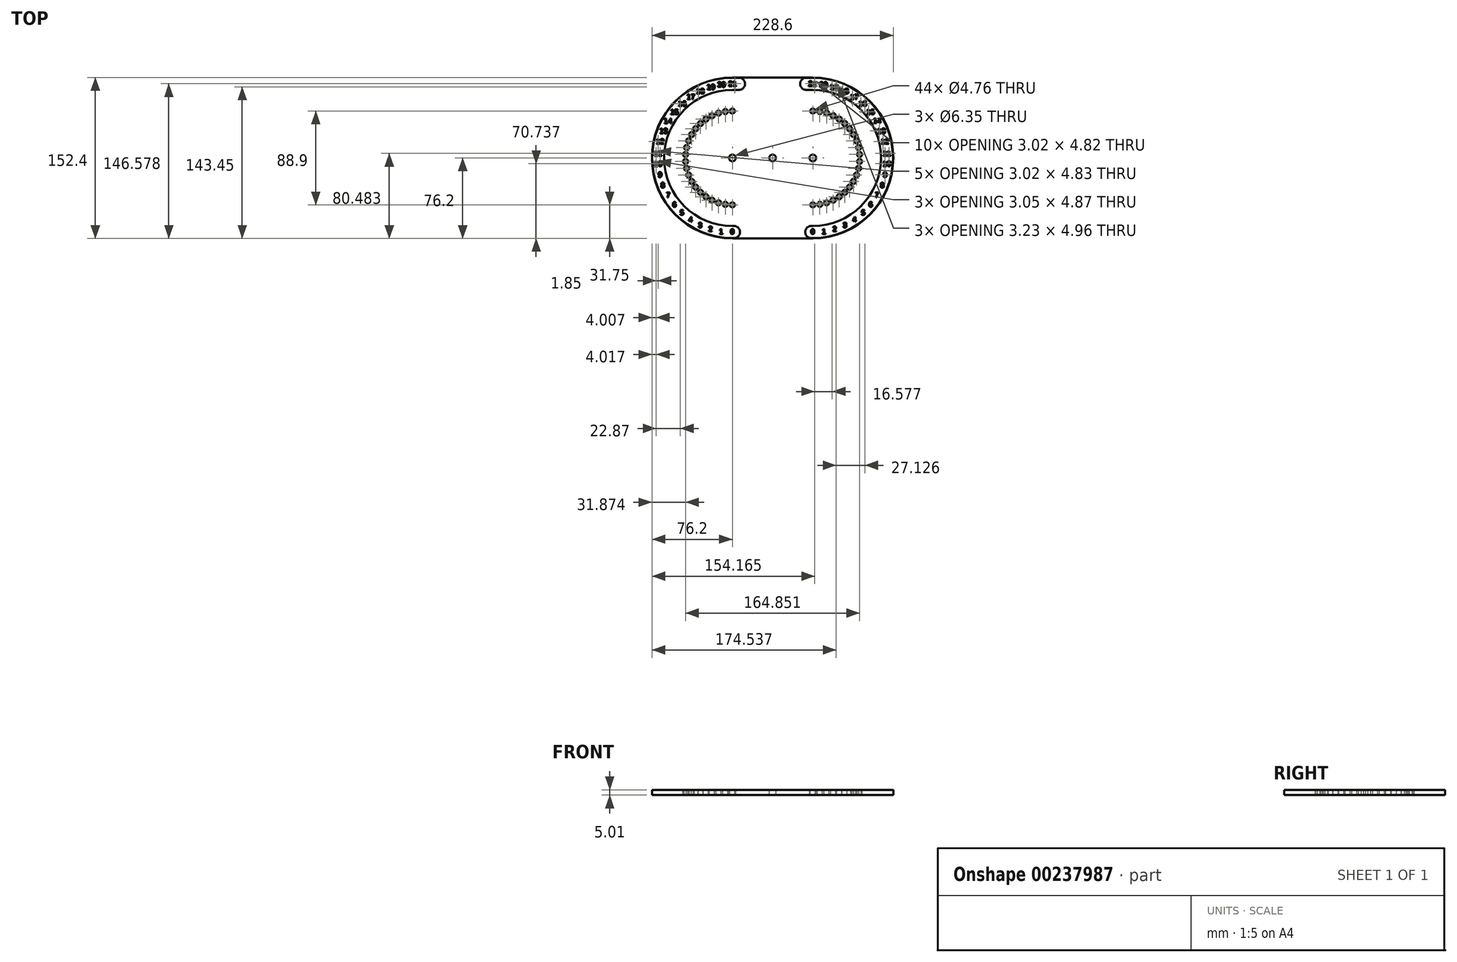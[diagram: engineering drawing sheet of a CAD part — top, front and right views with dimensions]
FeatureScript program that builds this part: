
annotation { "Feature Type Name" : "Feature", "Feature Type Description" : "" }
export const myFeature = defineFeature(function(context is Context, id is Id, definition is map)
    precondition{}
    {
        {
            var Q0;
            Q0=qCreatedBy(makeId("Top.planeOp"),FACE);
            var sketch = newSketch(context, id + "F0", { "sketchPlane" : qUnion([Q0])});
            skCircle(sketch, "E0", {"center": v(0, 0) * mm, "radius": 3.18 * mm});
            skLineSegment(sketch, "E1", {"start": v(0, 0) * mm, "end": v(38.1, 0) * mm, "construction": true});
            skLineSegment(sketch, "E2", {"start": v(0, 0) * mm, "end": v(-38.1, 0) * mm, "construction": true});
            skCircle(sketch, "E3", {"center": v(38.1, 0) * mm, "radius": 3.18 * mm});
            skCircle(sketch, "E4", {"center": v(-38.1, 0) * mm, "radius": 3.18 * mm});
            skCircle(sketch, "E5", {"center": v(38.1, 0) * mm, "radius": 44.45 * mm, "construction": true});
            skCircle(sketch, "E6", {"center": v(-38.1, 0) * mm, "radius": 44.45 * mm, "construction": true});
            skLineSegment(sketch, "E7.bottom", {"start": v(114.3, -76.2) * mm, "end": v(-114.3, -76.2) * mm});
            skLineSegment(sketch, "E7.top", {"start": v(114.3, 76.2) * mm, "end": v(-114.3, 76.2) * mm});
            skLineSegment(sketch, "E7.left", {"start": v(114.3, -76.2) * mm, "end": v(114.3, 76.2) * mm});
            skLineSegment(sketch, "E7.right", {"start": v(-114.3, -76.2) * mm, "end": v(-114.3, 76.2) * mm});
            skPoint(sketch, "E8", {"position": v(-114.3, 0) * mm});
            skSolve(sketch);
        }
        {
            var Q0;
            Q0 = qSketchRegion(id + "F0", true);
            extrude(context, id + "F1", {"entities" : qUnion([Q0]), "oppositeDirection" : true, "depth" : 4.76 * mm});
        }
        {
            var Q0;
            Q0=makeQuery(id+"F0.imprint","IMPRINT",FACE,{"disambiguationData":[TD([[makeQuery(id+"F0.imprint","IMPRINT",EDGE,{"derivedFrom":sQuery(id+"F0.wireOp",EDGE,"E0")}),-1.0]])]});
            var sketch = newSketch(context, id + "F2", { "sketchPlane" : qUnion([Q0])});
            skCircle(sketch, "E9", {"center": v(38.1, 44.45) * mm, "radius": 2.38 * mm});
            skLineSegment(sketch, "E10", {"start": v(38.1, 0) * mm, "end": v(38.1, 44.45) * mm, "construction": true});
            skSolve(sketch);
        }
        {
            var Q0;
            Q0 = qSketchRegion(id + "F2", true);
            extrude(context, id + "F3", {"entities" : qUnion([Q0]), "endBound" : BoundingType.SYMMETRIC, "oppositeDirection" : true, "depth" : 25.4 * mm});
        }
        {
            var Q0;
            Q0=makeQuery(id+"F3.opExtrude","SWEPT_BODY",BODY,{"disambiguationData":[OSD([sQuery(id+"F2.wireOp",EDGE,"E9")])]});
            var Q1;
            Q1=makeQuery(id+"F1.opExtrude","SWEPT_FACE",FACE,{"disambiguationData":[OSD([sQuery(id+"F0.wireOp",EDGE,"E3")])]});
            circularPattern(context, id + "F4", {"entities" : qUnion([Q0]), "axis" : qUnion([Q1]), "angle" : 180 * degree, "instanceCount" : 22, "equalSpace" : true});
        }
        {
            var Q0;
            Q0=makeQuery(id+"F4.opPattern","COPY",BODY,{"derivedFrom":makeQuery(id+"F3.opExtrude","SWEPT_BODY",BODY,{"disambiguationData":[OSD([sQuery(id+"F2.wireOp",EDGE,"E9")])]}),"instanceName":"10"});
            var Q1;
            Q1=makeQuery(id+"F4.opPattern","COPY",BODY,{"derivedFrom":makeQuery(id+"F3.opExtrude","SWEPT_BODY",BODY,{"disambiguationData":[OSD([sQuery(id+"F2.wireOp",EDGE,"E9")])]}),"instanceName":"11"});
            var Q2;
            Q2=makeQuery(id+"F4.opPattern","COPY",BODY,{"derivedFrom":makeQuery(id+"F3.opExtrude","SWEPT_BODY",BODY,{"disambiguationData":[OSD([sQuery(id+"F2.wireOp",EDGE,"E9")])]}),"instanceName":"12"});
            var Q3;
            Q3=makeQuery(id+"F4.opPattern","COPY",BODY,{"derivedFrom":makeQuery(id+"F3.opExtrude","SWEPT_BODY",BODY,{"disambiguationData":[OSD([sQuery(id+"F2.wireOp",EDGE,"E9")])]}),"instanceName":"13"});
            var Q4;
            Q4=makeQuery(id+"F4.opPattern","COPY",BODY,{"derivedFrom":makeQuery(id+"F3.opExtrude","SWEPT_BODY",BODY,{"disambiguationData":[OSD([sQuery(id+"F2.wireOp",EDGE,"E9")])]}),"instanceName":"14"});
            var Q5;
            Q5=makeQuery(id+"F4.opPattern","COPY",BODY,{"derivedFrom":makeQuery(id+"F3.opExtrude","SWEPT_BODY",BODY,{"disambiguationData":[OSD([sQuery(id+"F2.wireOp",EDGE,"E9")])]}),"instanceName":"15"});
            var Q6;
            Q6=makeQuery(id+"F4.opPattern","COPY",BODY,{"derivedFrom":makeQuery(id+"F3.opExtrude","SWEPT_BODY",BODY,{"disambiguationData":[OSD([sQuery(id+"F2.wireOp",EDGE,"E9")])]}),"instanceName":"16"});
            var Q7;
            Q7=makeQuery(id+"F4.opPattern","COPY",BODY,{"derivedFrom":makeQuery(id+"F3.opExtrude","SWEPT_BODY",BODY,{"disambiguationData":[OSD([sQuery(id+"F2.wireOp",EDGE,"E9")])]}),"instanceName":"17"});
            var Q8;
            Q8=makeQuery(id+"F4.opPattern","COPY",BODY,{"derivedFrom":makeQuery(id+"F3.opExtrude","SWEPT_BODY",BODY,{"disambiguationData":[OSD([sQuery(id+"F2.wireOp",EDGE,"E9")])]}),"instanceName":"18"});
            var Q9;
            Q9=makeQuery(id+"F4.opPattern","COPY",BODY,{"derivedFrom":makeQuery(id+"F3.opExtrude","SWEPT_BODY",BODY,{"disambiguationData":[OSD([sQuery(id+"F2.wireOp",EDGE,"E9")])]}),"instanceName":"19"});
            var Q10;
            Q10=makeQuery(id+"F4.opPattern","COPY",BODY,{"derivedFrom":makeQuery(id+"F3.opExtrude","SWEPT_BODY",BODY,{"disambiguationData":[OSD([sQuery(id+"F2.wireOp",EDGE,"E9")])]}),"instanceName":"20"});
            var Q11;
            Q11=makeQuery(id+"F4.opPattern","COPY",BODY,{"derivedFrom":makeQuery(id+"F3.opExtrude","SWEPT_BODY",BODY,{"disambiguationData":[OSD([sQuery(id+"F2.wireOp",EDGE,"E9")])]}),"instanceName":"1"});
            var Q12;
            Q12=makeQuery(id+"F3.opExtrude","SWEPT_BODY",BODY,{"disambiguationData":[OSD([sQuery(id+"F2.wireOp",EDGE,"E9")])]});
            var Q13;
            Q13=makeQuery(id+"F4.opPattern","COPY",BODY,{"derivedFrom":makeQuery(id+"F3.opExtrude","SWEPT_BODY",BODY,{"disambiguationData":[OSD([sQuery(id+"F2.wireOp",EDGE,"E9")])]}),"instanceName":"3"});
            var Q14;
            Q14=makeQuery(id+"F4.opPattern","COPY",BODY,{"derivedFrom":makeQuery(id+"F3.opExtrude","SWEPT_BODY",BODY,{"disambiguationData":[OSD([sQuery(id+"F2.wireOp",EDGE,"E9")])]}),"instanceName":"2"});
            var Q15;
            Q15=makeQuery(id+"F4.opPattern","COPY",BODY,{"derivedFrom":makeQuery(id+"F3.opExtrude","SWEPT_BODY",BODY,{"disambiguationData":[OSD([sQuery(id+"F2.wireOp",EDGE,"E9")])]}),"instanceName":"4"});
            var Q16;
            Q16=makeQuery(id+"F4.opPattern","COPY",BODY,{"derivedFrom":makeQuery(id+"F3.opExtrude","SWEPT_BODY",BODY,{"disambiguationData":[OSD([sQuery(id+"F2.wireOp",EDGE,"E9")])]}),"instanceName":"5"});
            var Q17;
            Q17=makeQuery(id+"F4.opPattern","COPY",BODY,{"derivedFrom":makeQuery(id+"F3.opExtrude","SWEPT_BODY",BODY,{"disambiguationData":[OSD([sQuery(id+"F2.wireOp",EDGE,"E9")])]}),"instanceName":"7"});
            var Q18;
            Q18=makeQuery(id+"F4.opPattern","COPY",BODY,{"derivedFrom":makeQuery(id+"F3.opExtrude","SWEPT_BODY",BODY,{"disambiguationData":[OSD([sQuery(id+"F2.wireOp",EDGE,"E9")])]}),"instanceName":"6"});
            var Q19;
            Q19=makeQuery(id+"F4.opPattern","COPY",BODY,{"derivedFrom":makeQuery(id+"F3.opExtrude","SWEPT_BODY",BODY,{"disambiguationData":[OSD([sQuery(id+"F2.wireOp",EDGE,"E9")])]}),"instanceName":"8"});
            var Q20;
            Q20=makeQuery(id+"F4.opPattern","COPY",BODY,{"derivedFrom":makeQuery(id+"F3.opExtrude","SWEPT_BODY",BODY,{"disambiguationData":[OSD([sQuery(id+"F2.wireOp",EDGE,"E9")])]}),"instanceName":"9"});
            var Q21;
            Q21=makeQuery(id+"F4.opPattern","COPY",BODY,{"derivedFrom":makeQuery(id+"F3.opExtrude","SWEPT_BODY",BODY,{"disambiguationData":[OSD([sQuery(id+"F2.wireOp",EDGE,"E9")])]}),"instanceName":"21"});
            var Q22;
            Q22=qCreatedBy(makeId("Right.planeOp"),FACE);
            mirror(context, id + "F5", {"entities" : qUnion([Q0, Q1, Q2, Q3, Q4, Q5, Q6, Q7, Q8, Q9, Q10, Q11, Q12, Q13, Q14, Q15, Q16, Q17, Q18, Q19, Q20, Q21]), "mirrorPlane" : qUnion([Q22])});
        }
        {
            var Q0;
            Q0=makeQuery(id+"F4.opPattern","COPY",BODY,{"derivedFrom":makeQuery(id+"F3.opExtrude","SWEPT_BODY",BODY,{"disambiguationData":[OSD([sQuery(id+"F2.wireOp",EDGE,"E9")])]}),"instanceName":"1"});
            var Q1;
            Q1=makeQuery(id+"F3.opExtrude","SWEPT_BODY",BODY,{"disambiguationData":[OSD([sQuery(id+"F2.wireOp",EDGE,"E9")])]});
            var Q2;
            Q2=makeQuery(id+"F4.opPattern","COPY",BODY,{"derivedFrom":makeQuery(id+"F3.opExtrude","SWEPT_BODY",BODY,{"disambiguationData":[OSD([sQuery(id+"F2.wireOp",EDGE,"E9")])]}),"instanceName":"3"});
            var Q3;
            Q3=makeQuery(id+"F4.opPattern","COPY",BODY,{"derivedFrom":makeQuery(id+"F3.opExtrude","SWEPT_BODY",BODY,{"disambiguationData":[OSD([sQuery(id+"F2.wireOp",EDGE,"E9")])]}),"instanceName":"2"});
            var Q4;
            Q4=makeQuery(id+"F4.opPattern","COPY",BODY,{"derivedFrom":makeQuery(id+"F3.opExtrude","SWEPT_BODY",BODY,{"disambiguationData":[OSD([sQuery(id+"F2.wireOp",EDGE,"E9")])]}),"instanceName":"4"});
            var Q5;
            Q5=makeQuery(id+"F4.opPattern","COPY",BODY,{"derivedFrom":makeQuery(id+"F3.opExtrude","SWEPT_BODY",BODY,{"disambiguationData":[OSD([sQuery(id+"F2.wireOp",EDGE,"E9")])]}),"instanceName":"5"});
            var Q6;
            Q6=makeQuery(id+"F5.opPattern","COPY",BODY,{"derivedFrom":makeQuery(id+"F4.opPattern","COPY",BODY,{"derivedFrom":makeQuery(id+"F3.opExtrude","SWEPT_BODY",BODY,{"disambiguationData":[OSD([sQuery(id+"F2.wireOp",EDGE,"E9")])]}),"instanceName":"3"}),"instanceName":"1"});
            var Q7;
            Q7=makeQuery(id+"F4.opPattern","COPY",BODY,{"derivedFrom":makeQuery(id+"F3.opExtrude","SWEPT_BODY",BODY,{"disambiguationData":[OSD([sQuery(id+"F2.wireOp",EDGE,"E9")])]}),"instanceName":"7"});
            var Q8;
            Q8=makeQuery(id+"F4.opPattern","COPY",BODY,{"derivedFrom":makeQuery(id+"F3.opExtrude","SWEPT_BODY",BODY,{"disambiguationData":[OSD([sQuery(id+"F2.wireOp",EDGE,"E9")])]}),"instanceName":"6"});
            var Q9;
            Q9=makeQuery(id+"F4.opPattern","COPY",BODY,{"derivedFrom":makeQuery(id+"F3.opExtrude","SWEPT_BODY",BODY,{"disambiguationData":[OSD([sQuery(id+"F2.wireOp",EDGE,"E9")])]}),"instanceName":"8"});
            var Q10;
            Q10=makeQuery(id+"F4.opPattern","COPY",BODY,{"derivedFrom":makeQuery(id+"F3.opExtrude","SWEPT_BODY",BODY,{"disambiguationData":[OSD([sQuery(id+"F2.wireOp",EDGE,"E9")])]}),"instanceName":"9"});
            var Q11;
            Q11=makeQuery(id+"F4.opPattern","COPY",BODY,{"derivedFrom":makeQuery(id+"F3.opExtrude","SWEPT_BODY",BODY,{"disambiguationData":[OSD([sQuery(id+"F2.wireOp",EDGE,"E9")])]}),"instanceName":"10"});
            var Q12;
            Q12=makeQuery(id+"F4.opPattern","COPY",BODY,{"derivedFrom":makeQuery(id+"F3.opExtrude","SWEPT_BODY",BODY,{"disambiguationData":[OSD([sQuery(id+"F2.wireOp",EDGE,"E9")])]}),"instanceName":"11"});
            var Q13;
            Q13=makeQuery(id+"F4.opPattern","COPY",BODY,{"derivedFrom":makeQuery(id+"F3.opExtrude","SWEPT_BODY",BODY,{"disambiguationData":[OSD([sQuery(id+"F2.wireOp",EDGE,"E9")])]}),"instanceName":"12"});
            var Q14;
            Q14=makeQuery(id+"F4.opPattern","COPY",BODY,{"derivedFrom":makeQuery(id+"F3.opExtrude","SWEPT_BODY",BODY,{"disambiguationData":[OSD([sQuery(id+"F2.wireOp",EDGE,"E9")])]}),"instanceName":"13"});
            var Q15;
            Q15=makeQuery(id+"F4.opPattern","COPY",BODY,{"derivedFrom":makeQuery(id+"F3.opExtrude","SWEPT_BODY",BODY,{"disambiguationData":[OSD([sQuery(id+"F2.wireOp",EDGE,"E9")])]}),"instanceName":"14"});
            var Q16;
            Q16=makeQuery(id+"F4.opPattern","COPY",BODY,{"derivedFrom":makeQuery(id+"F3.opExtrude","SWEPT_BODY",BODY,{"disambiguationData":[OSD([sQuery(id+"F2.wireOp",EDGE,"E9")])]}),"instanceName":"15"});
            var Q17;
            Q17=makeQuery(id+"F4.opPattern","COPY",BODY,{"derivedFrom":makeQuery(id+"F3.opExtrude","SWEPT_BODY",BODY,{"disambiguationData":[OSD([sQuery(id+"F2.wireOp",EDGE,"E9")])]}),"instanceName":"16"});
            var Q18;
            Q18=makeQuery(id+"F4.opPattern","COPY",BODY,{"derivedFrom":makeQuery(id+"F3.opExtrude","SWEPT_BODY",BODY,{"disambiguationData":[OSD([sQuery(id+"F2.wireOp",EDGE,"E9")])]}),"instanceName":"17"});
            var Q19;
            Q19=makeQuery(id+"F4.opPattern","COPY",BODY,{"derivedFrom":makeQuery(id+"F3.opExtrude","SWEPT_BODY",BODY,{"disambiguationData":[OSD([sQuery(id+"F2.wireOp",EDGE,"E9")])]}),"instanceName":"18"});
            var Q20;
            Q20=makeQuery(id+"F4.opPattern","COPY",BODY,{"derivedFrom":makeQuery(id+"F3.opExtrude","SWEPT_BODY",BODY,{"disambiguationData":[OSD([sQuery(id+"F2.wireOp",EDGE,"E9")])]}),"instanceName":"19"});
            var Q21;
            Q21=makeQuery(id+"F4.opPattern","COPY",BODY,{"derivedFrom":makeQuery(id+"F3.opExtrude","SWEPT_BODY",BODY,{"disambiguationData":[OSD([sQuery(id+"F2.wireOp",EDGE,"E9")])]}),"instanceName":"20"});
            var Q22;
            Q22=makeQuery(id+"F5.opPattern","COPY",BODY,{"derivedFrom":makeQuery(id+"F4.opPattern","COPY",BODY,{"derivedFrom":makeQuery(id+"F3.opExtrude","SWEPT_BODY",BODY,{"disambiguationData":[OSD([sQuery(id+"F2.wireOp",EDGE,"E9")])]}),"instanceName":"2"}),"instanceName":"1"});
            var Q23;
            Q23=makeQuery(id+"F5.opPattern","COPY",BODY,{"derivedFrom":makeQuery(id+"F4.opPattern","COPY",BODY,{"derivedFrom":makeQuery(id+"F3.opExtrude","SWEPT_BODY",BODY,{"disambiguationData":[OSD([sQuery(id+"F2.wireOp",EDGE,"E9")])]}),"instanceName":"1"}),"instanceName":"1"});
            var Q24;
            Q24=makeQuery(id+"F5.opPattern","COPY",BODY,{"derivedFrom":makeQuery(id+"F4.opPattern","COPY",BODY,{"derivedFrom":makeQuery(id+"F3.opExtrude","SWEPT_BODY",BODY,{"disambiguationData":[OSD([sQuery(id+"F2.wireOp",EDGE,"E9")])]}),"instanceName":"4"}),"instanceName":"1"});
            var Q25;
            Q25=makeQuery(id+"F5.opPattern","COPY",BODY,{"derivedFrom":makeQuery(id+"F4.opPattern","COPY",BODY,{"derivedFrom":makeQuery(id+"F3.opExtrude","SWEPT_BODY",BODY,{"disambiguationData":[OSD([sQuery(id+"F2.wireOp",EDGE,"E9")])]}),"instanceName":"5"}),"instanceName":"1"});
            var Q26;
            Q26=makeQuery(id+"F5.opPattern","COPY",BODY,{"derivedFrom":makeQuery(id+"F4.opPattern","COPY",BODY,{"derivedFrom":makeQuery(id+"F3.opExtrude","SWEPT_BODY",BODY,{"disambiguationData":[OSD([sQuery(id+"F2.wireOp",EDGE,"E9")])]}),"instanceName":"6"}),"instanceName":"1"});
            var Q27;
            Q27=makeQuery(id+"F5.opPattern","COPY",BODY,{"derivedFrom":makeQuery(id+"F4.opPattern","COPY",BODY,{"derivedFrom":makeQuery(id+"F3.opExtrude","SWEPT_BODY",BODY,{"disambiguationData":[OSD([sQuery(id+"F2.wireOp",EDGE,"E9")])]}),"instanceName":"10"}),"instanceName":"1"});
            var Q28;
            Q28=makeQuery(id+"F5.opPattern","COPY",BODY,{"derivedFrom":makeQuery(id+"F4.opPattern","COPY",BODY,{"derivedFrom":makeQuery(id+"F3.opExtrude","SWEPT_BODY",BODY,{"disambiguationData":[OSD([sQuery(id+"F2.wireOp",EDGE,"E9")])]}),"instanceName":"11"}),"instanceName":"1"});
            var Q29;
            Q29=makeQuery(id+"F5.opPattern","COPY",BODY,{"derivedFrom":makeQuery(id+"F4.opPattern","COPY",BODY,{"derivedFrom":makeQuery(id+"F3.opExtrude","SWEPT_BODY",BODY,{"disambiguationData":[OSD([sQuery(id+"F2.wireOp",EDGE,"E9")])]}),"instanceName":"12"}),"instanceName":"1"});
            var Q30;
            Q30=makeQuery(id+"F5.opPattern","COPY",BODY,{"derivedFrom":makeQuery(id+"F4.opPattern","COPY",BODY,{"derivedFrom":makeQuery(id+"F3.opExtrude","SWEPT_BODY",BODY,{"disambiguationData":[OSD([sQuery(id+"F2.wireOp",EDGE,"E9")])]}),"instanceName":"13"}),"instanceName":"1"});
            var Q31;
            Q31=makeQuery(id+"F5.opPattern","COPY",BODY,{"derivedFrom":makeQuery(id+"F4.opPattern","COPY",BODY,{"derivedFrom":makeQuery(id+"F3.opExtrude","SWEPT_BODY",BODY,{"disambiguationData":[OSD([sQuery(id+"F2.wireOp",EDGE,"E9")])]}),"instanceName":"14"}),"instanceName":"1"});
            var Q32;
            Q32=makeQuery(id+"F5.opPattern","COPY",BODY,{"derivedFrom":makeQuery(id+"F4.opPattern","COPY",BODY,{"derivedFrom":makeQuery(id+"F3.opExtrude","SWEPT_BODY",BODY,{"disambiguationData":[OSD([sQuery(id+"F2.wireOp",EDGE,"E9")])]}),"instanceName":"15"}),"instanceName":"1"});
            var Q33;
            Q33=makeQuery(id+"F5.opPattern","COPY",BODY,{"derivedFrom":makeQuery(id+"F4.opPattern","COPY",BODY,{"derivedFrom":makeQuery(id+"F3.opExtrude","SWEPT_BODY",BODY,{"disambiguationData":[OSD([sQuery(id+"F2.wireOp",EDGE,"E9")])]}),"instanceName":"16"}),"instanceName":"1"});
            var Q34;
            Q34=makeQuery(id+"F5.opPattern","COPY",BODY,{"derivedFrom":makeQuery(id+"F4.opPattern","COPY",BODY,{"derivedFrom":makeQuery(id+"F3.opExtrude","SWEPT_BODY",BODY,{"disambiguationData":[OSD([sQuery(id+"F2.wireOp",EDGE,"E9")])]}),"instanceName":"17"}),"instanceName":"1"});
            var Q35;
            Q35=makeQuery(id+"F5.opPattern","COPY",BODY,{"derivedFrom":makeQuery(id+"F4.opPattern","COPY",BODY,{"derivedFrom":makeQuery(id+"F3.opExtrude","SWEPT_BODY",BODY,{"disambiguationData":[OSD([sQuery(id+"F2.wireOp",EDGE,"E9")])]}),"instanceName":"18"}),"instanceName":"1"});
            var Q36;
            Q36=makeQuery(id+"F5.opPattern","COPY",BODY,{"derivedFrom":makeQuery(id+"F4.opPattern","COPY",BODY,{"derivedFrom":makeQuery(id+"F3.opExtrude","SWEPT_BODY",BODY,{"disambiguationData":[OSD([sQuery(id+"F2.wireOp",EDGE,"E9")])]}),"instanceName":"19"}),"instanceName":"1"});
            var Q37;
            Q37=makeQuery(id+"F5.opPattern","COPY",BODY,{"derivedFrom":makeQuery(id+"F4.opPattern","COPY",BODY,{"derivedFrom":makeQuery(id+"F3.opExtrude","SWEPT_BODY",BODY,{"disambiguationData":[OSD([sQuery(id+"F2.wireOp",EDGE,"E9")])]}),"instanceName":"20"}),"instanceName":"1"});
            var Q38;
            Q38=makeQuery(id+"F5.opPattern","COPY",BODY,{"derivedFrom":makeQuery(id+"F3.opExtrude","SWEPT_BODY",BODY,{"disambiguationData":[OSD([sQuery(id+"F2.wireOp",EDGE,"E9")])]}),"instanceName":"1"});
            var Q39;
            Q39=makeQuery(id+"F5.opPattern","COPY",BODY,{"derivedFrom":makeQuery(id+"F4.opPattern","COPY",BODY,{"derivedFrom":makeQuery(id+"F3.opExtrude","SWEPT_BODY",BODY,{"disambiguationData":[OSD([sQuery(id+"F2.wireOp",EDGE,"E9")])]}),"instanceName":"7"}),"instanceName":"1"});
            var Q40;
            Q40=makeQuery(id+"F5.opPattern","COPY",BODY,{"derivedFrom":makeQuery(id+"F4.opPattern","COPY",BODY,{"derivedFrom":makeQuery(id+"F3.opExtrude","SWEPT_BODY",BODY,{"disambiguationData":[OSD([sQuery(id+"F2.wireOp",EDGE,"E9")])]}),"instanceName":"8"}),"instanceName":"1"});
            var Q41;
            Q41=makeQuery(id+"F5.opPattern","COPY",BODY,{"derivedFrom":makeQuery(id+"F4.opPattern","COPY",BODY,{"derivedFrom":makeQuery(id+"F3.opExtrude","SWEPT_BODY",BODY,{"disambiguationData":[OSD([sQuery(id+"F2.wireOp",EDGE,"E9")])]}),"instanceName":"9"}),"instanceName":"1"});
            var Q42;
            Q42=makeQuery(id+"F4.opPattern","COPY",BODY,{"derivedFrom":makeQuery(id+"F3.opExtrude","SWEPT_BODY",BODY,{"disambiguationData":[OSD([sQuery(id+"F2.wireOp",EDGE,"E9")])]}),"instanceName":"21"});
            var Q43;
            Q43=makeQuery(id+"F5.opPattern","COPY",BODY,{"derivedFrom":makeQuery(id+"F4.opPattern","COPY",BODY,{"derivedFrom":makeQuery(id+"F3.opExtrude","SWEPT_BODY",BODY,{"disambiguationData":[OSD([sQuery(id+"F2.wireOp",EDGE,"E9")])]}),"instanceName":"21"}),"instanceName":"1"});
            var Q44;
            Q44=makeQuery(id+"F1.opExtrude","SWEPT_BODY",BODY,{"disambiguationData":[OSD([sQuery(id+"F0.wireOp",EDGE,"E0"),sQuery(id+"F0.wireOp",EDGE,"E3"),sQuery(id+"F0.wireOp",EDGE,"E4"),sQuery(id+"F0.wireOp",EDGE,"E7.bottom"),sQuery(id+"F0.wireOp",EDGE,"E7.top"),sQuery(id+"F0.wireOp",EDGE,"E7.left"),sQuery(id+"F0.wireOp",EDGE,"E7.right")])]});
            booleanBodies(context, id + "F6", {"operationType" : BooleanOperationType.SUBTRACTION, "tools" : qUnion([Q0, Q1, Q2, Q3, Q4, Q5, Q6, Q7, Q8, Q9, Q10, Q11, Q12, Q13, Q14, Q15, Q16, Q17, Q18, Q19, Q20, Q21, Q22, Q23, Q24, Q25, Q26, Q27, Q28, Q29, Q30, Q31, Q32, Q33, Q34, Q35, Q36, Q37, Q38, Q39, Q40, Q41, Q42, Q43]), "targets" : qUnion([Q44])});
        }
        {
            var Q0;
            Q0=makeQuery(id+"F1.opExtrude","SWEPT_EDGE",EDGE,{"disambiguationData":[OSD([sQuery(id+"F0.wireOp",EDGE,"E7.bottom"),sQuery(id+"F0.wireOp",EDGE,"E7.right")])]});
            var Q1;
            Q1=makeQuery(id+"F1.opExtrude","SWEPT_EDGE",EDGE,{"disambiguationData":[OSD([sQuery(id+"F0.wireOp",EDGE,"E7.top"),sQuery(id+"F0.wireOp",EDGE,"E7.right")])]});
            var Q2;
            Q2=makeQuery(id+"F1.opExtrude","SWEPT_EDGE",EDGE,{"disambiguationData":[OSD([sQuery(id+"F0.wireOp",EDGE,"E7.top"),sQuery(id+"F0.wireOp",EDGE,"E7.left")])]});
            var Q3;
            Q3=makeQuery(id+"F1.opExtrude","SWEPT_EDGE",EDGE,{"disambiguationData":[OSD([sQuery(id+"F0.wireOp",EDGE,"E7.bottom"),sQuery(id+"F0.wireOp",EDGE,"E7.left")])]});
            fillet(context, id + "F7", {"entities" : qUnion([Q0, Q1, Q2, Q3]), "radius" : 76.2 * mm, "tangentPropagation" : true, "allowEdgeOverflow" : false});
        }
        {
            var Q0;
            Q0=makeQuery(id+"F1.opExtrude","CAP_FACE",FACE,{"disambiguationData":[OSD([sQuery(id+"F0.wireOp",EDGE,"E0"),sQuery(id+"F0.wireOp",EDGE,"E3"),sQuery(id+"F0.wireOp",EDGE,"E4"),sQuery(id+"F0.wireOp",EDGE,"E7.bottom"),sQuery(id+"F0.wireOp",EDGE,"E7.top"),sQuery(id+"F0.wireOp",EDGE,"E7.left"),sQuery(id+"F0.wireOp",EDGE,"E7.right")])],"isStart":true});
            var sketch = newSketch(context, id + "F8", { "sketchPlane" : qUnion([Q0])});
            skText(sketch, "E11", { "text": "21", "fontName": "Arimo-Regular.ttf"});
            skText(sketch, "E12", { "text": "20", "fontName": "Arimo-Regular.ttf"});
            skText(sketch, "E13", { "text": "19", "fontName": "Arimo-Regular.ttf"});
            skText(sketch, "E14", { "text": "17", "fontName": "Arimo-Regular.ttf"});
            skText(sketch, "E15", { "text": "14", "fontName": "Arimo-Regular.ttf"});
            skText(sketch, "E16", { "text": "15", "fontName": "Arimo-Regular.ttf"});
            skText(sketch, "E17", { "text": "7", "fontName": "Arimo-Regular.ttf"});
            skText(sketch, "E18", { "text": "13", "fontName": "Arimo-Regular.ttf"});
            skText(sketch, "E19", { "text": "18\n", "fontName": "Arimo-Regular.ttf"});
            skText(sketch, "E20", { "text": "8", "fontName": "Arimo-Regular.ttf"});
            skText(sketch, "E21", { "text": "16", "fontName": "Arimo-Regular.ttf"});
            skText(sketch, "E22", { "text": "11", "fontName": "Arimo-Regular.ttf"});
            skText(sketch, "E23", { "text": "9", "fontName": "Arimo-Regular.ttf"});
            skText(sketch, "E24", { "text": "12", "fontName": "Arimo-Regular.ttf"});
            skText(sketch, "E25", { "text": "10", "fontName": "Arimo-Regular.ttf"});
            skText(sketch, "E26", { "text": "0", "fontName": "Arimo-Regular.ttf"});
            skText(sketch, "E27", { "text": "4", "fontName": "Arimo-Regular.ttf"});
            skText(sketch, "E28", { "text": "2", "fontName": "Arimo-Regular.ttf"});
            skText(sketch, "E29", { "text": "6", "fontName": "Arimo-Regular.ttf"});
            skText(sketch, "E30", { "text": "3", "fontName": "Arimo-Regular.ttf"});
            skText(sketch, "E31", { "text": "1", "fontName": "Arimo-Regular.ttf"});
            skText(sketch, "E32", { "text": "5", "fontName": "Arimo-Regular.ttf"});
            skArc(sketch, "E33.0", {"start": v(38.1, -75.95) * mm, "mid": v(114.05, 0) * mm, "end": v(38.1, 75.95) * mm});
            skLineSegment(sketch, "E34", {"start": v(38.1, 75.95) * mm, "end": v(31.75, 75.95) * mm});
            skLineSegment(sketch, "E35", {"start": v(38.1, -75.95) * mm, "end": v(36.58, -75.95) * mm});
            skLineSegment(sketch, "E36.0", {"start": v(38.1, -64.52) * mm, "end": v(36.58, -64.52) * mm});
            skArc(sketch, "E36.1", {"start": v(38.1, -64.52) * mm, "mid": v(102.62, 0) * mm, "end": v(38.1, 64.52) * mm});
            skLineSegment(sketch, "E36.2", {"start": v(38.1, 64.52) * mm, "end": v(31.75, 64.52) * mm});
            skArc(sketch, "E37", {"start": v(31.75, 75.95) * mm, "mid": v(26.04, 70.23) * mm, "end": v(31.75, 64.52) * mm});
            skArc(sketch, "E38", {"start": v(36.58, -64.52) * mm, "mid": v(30.86, -70.23) * mm, "end": v(36.58, -75.95) * mm});
            skLineSegment(sketch, "E39", {"start": v(38.1, 0) * mm, "end": v(38.1, 44.45) * mm, "construction": true});
            skLineSegment(sketch, "E40", {"start": v(38.1, 0) * mm, "end": v(44.72, 43.95) * mm, "construction": true});
            skLineSegment(sketch, "E41", {"start": v(38.1, 0) * mm, "end": v(51.2, 42.48) * mm, "construction": true});
            skLineSegment(sketch, "E42", {"start": v(51.2, 42.48) * mm, "end": v(60.49, 72.57) * mm, "construction": true});
            skLineSegment(sketch, "E43", {"start": v(38.1, 0) * mm, "end": v(57.39, 40.05) * mm, "construction": true});
            skLineSegment(sketch, "E44", {"start": v(57.39, 40.05) * mm, "end": v(71.05, 68.42) * mm, "construction": true});
            skLineSegment(sketch, "E45", {"start": v(38.1, 0) * mm, "end": v(63.14, 36.73) * mm, "construction": true});
            skLineSegment(sketch, "E46", {"start": v(63.14, 36.73) * mm, "end": v(80.88, 62.75) * mm, "construction": true});
            skLineSegment(sketch, "E47", {"start": v(38.1, 0) * mm, "end": v(68.33, 32.58) * mm, "construction": true});
            skLineSegment(sketch, "E48", {"start": v(68.33, 32.58) * mm, "end": v(89.76, 55.67) * mm, "construction": true});
            skLineSegment(sketch, "E49", {"start": v(38.1, 0) * mm, "end": v(72.85, 27.71) * mm, "construction": true});
            skLineSegment(sketch, "E50", {"start": v(72.85, 27.71) * mm, "end": v(97.48, 47.35) * mm, "construction": true});
            skLineSegment(sketch, "E51", {"start": v(38.1, 0) * mm, "end": v(76.6, 22.23) * mm, "construction": true});
            skLineSegment(sketch, "E52", {"start": v(76.6, 22.22) * mm, "end": v(103.87, 37.97) * mm, "construction": true});
            skLineSegment(sketch, "E53", {"start": v(38.1, 0) * mm, "end": v(79.48, 16.24) * mm, "construction": true});
            skLineSegment(sketch, "E54", {"start": v(79.48, 16.24) * mm, "end": v(108.8, 27.75) * mm, "construction": true});
            skLineSegment(sketch, "E55", {"start": v(38.1, 0) * mm, "end": v(81.44, 9.9) * mm, "construction": true});
            skLineSegment(sketch, "E56", {"start": v(81.44, 9.9) * mm, "end": v(112.14, 16.9) * mm, "construction": true});
            skLineSegment(sketch, "E57", {"start": v(38.1, 0) * mm, "end": v(82.43, 3.32) * mm, "construction": true});
            skLineSegment(sketch, "E58", {"start": v(82.43, 3.32) * mm, "end": v(113.83, 5.68) * mm, "construction": true});
            skLineSegment(sketch, "E59", {"start": v(38.1, 0) * mm, "end": v(82.43, -3.32) * mm, "construction": true});
            skLineSegment(sketch, "E60", {"start": v(82.43, -3.32) * mm, "end": v(113.83, -5.68) * mm, "construction": true});
            skLineSegment(sketch, "E61", {"start": v(38.1, 0) * mm, "end": v(81.44, -9.9) * mm, "construction": true});
            skLineSegment(sketch, "E62", {"start": v(81.44, -9.9) * mm, "end": v(112.14, -16.9) * mm, "construction": true});
            skLineSegment(sketch, "E63", {"start": v(38.1, 0) * mm, "end": v(79.48, -16.24) * mm, "construction": true});
            skLineSegment(sketch, "E64", {"start": v(79.48, -16.24) * mm, "end": v(108.8, -27.75) * mm, "construction": true});
            skLineSegment(sketch, "E65", {"start": v(38.1, 0) * mm, "end": v(76.6, -22.23) * mm, "construction": true});
            skLineSegment(sketch, "E66", {"start": v(76.6, -22.23) * mm, "end": v(103.87, -37.97) * mm, "construction": true});
            skLineSegment(sketch, "E67", {"start": v(38.1, 0) * mm, "end": v(72.85, -27.71) * mm, "construction": true});
            skLineSegment(sketch, "E68", {"start": v(72.85, -27.71) * mm, "end": v(97.48, -47.35) * mm, "construction": true});
            skLineSegment(sketch, "E69", {"start": v(38.1, 0) * mm, "end": v(68.33, -32.58) * mm, "construction": true});
            skLineSegment(sketch, "E70", {"start": v(68.33, -32.58) * mm, "end": v(89.76, -55.67) * mm, "construction": true});
            skLineSegment(sketch, "E71", {"start": v(38.1, 0) * mm, "end": v(63.14, -36.73) * mm, "construction": true});
            skLineSegment(sketch, "E72", {"start": v(63.14, -36.73) * mm, "end": v(80.88, -62.75) * mm, "construction": true});
            skLineSegment(sketch, "E73", {"start": v(38.1, 0) * mm, "end": v(57.39, -40.05) * mm, "construction": true});
            skLineSegment(sketch, "E74", {"start": v(57.39, -40.05) * mm, "end": v(71.05, -68.42) * mm, "construction": true});
            skLineSegment(sketch, "E75", {"start": v(38.1, 0) * mm, "end": v(51.2, -42.48) * mm, "construction": true});
            skLineSegment(sketch, "E76", {"start": v(51.2, -42.48) * mm, "end": v(60.49, -72.57) * mm, "construction": true});
            skLineSegment(sketch, "E77", {"start": v(38.1, 0) * mm, "end": v(44.72, -43.95) * mm, "construction": true});
            skLineSegment(sketch, "E78", {"start": v(44.72, -43.95) * mm, "end": v(49.42, -75.1) * mm, "construction": true});
            skLineSegment(sketch, "E79", {"start": v(38.1, 0) * mm, "end": v(38.1, -44.45) * mm, "construction": true});
            skLineSegment(sketch, "E80", {"start": v(38.1, -44.45) * mm, "end": v(38.1, -75.95) * mm, "construction": true});
            skLineSegment(sketch, "E81", {"start": v(44.72, 43.95) * mm, "end": v(49.42, 75.1) * mm, "construction": true});
            skLineSegment(sketch, "E82", {"start": v(38.1, 44.45) * mm, "end": v(38.1, 75.95) * mm, "construction": true});
            const initialGuessF8  = {"E11": [0.03393, 0.06797, 1, 0, 0.00504], "E12": [0.04434, 0.06718, 1, 0, 0.005], "E13": [0.0544, 0.06484, 1, 0, 0.00504], "E14": [0.07357, 0.05546, 1, 0, 0.00504], "E15": [0.09513, 0.03284, 1, 0, 0.00496], "E16": [0.08891, 0.04127, 1, 0, 0.00504], "E17": [0.0968, -0.03738, 1, 0, 0.00497], "E18": [0.0992, 0.0232, 1, 0, 0.00504], "E19": [0.06436, 0.06093, 1, 0, 0.00504], "E20": [0.102, -0.0281, 1, 0, 0.0049], "E21": [0.0815, 0.04909, 1, 0, 0.00504], "E22": [0.10442, 0.0019, 1, 0, 0.00504], "E23": [0.10457, -0.01825, 1, 0, 0.00504], "E24": [0.10256, 0.0132, 1, 0, 0.00505], "E25": [0.10436, -0.00786, 1, 0, 0.00504], "E26": [0.03612, -0.07208, 1, 0, 0.00487], "E27": [0.0758, -0.0606, 1, 0, 0.0048], "E28": [0.05683, -0.06966, 1, 0, 0.00497], "E29": [0.09098, -0.04641, 1, 0, 0.00491], "E30": [0.06662, -0.06592, 1, 0, 0.00491], "E31": [0.04676, -0.07208, 1, 0, 0.00495], "E32": [0.0839, -0.05405, 1, 0, 0.0049]};
            skSetInitialGuess(sketch, initialGuessF8);
            skSolve(sketch);
        }
        {
            var Q0;
            Q0 = qSketchRegion(id + "F8", true);
            var Q1;
            Q1=makeQuery(id+"F8.imprint","IMPRINT",FACE,{"disambiguationData":[TD([[makeQuery(id+"F8.imprint","IMPRINT",EDGE,{"derivedFrom":sQuery(id+"F8.wireOp",EDGE,"E12.sketch_text.stroke-32")}),1.0]])]});
            var Q2;
            Q2=makeQuery(id+"F8.imprint","IMPRINT",FACE,{"disambiguationData":[TD([[makeQuery(id+"F8.imprint","IMPRINT",EDGE,{"derivedFrom":sQuery(id+"F8.wireOp",EDGE,"E13.sketch_text.stroke-27")}),1.0]])]});
            var Q3;
            Q3=makeQuery(id+"F8.imprint","IMPRINT",FACE,{"disambiguationData":[TD([[makeQuery(id+"F8.imprint","IMPRINT",EDGE,{"derivedFrom":sQuery(id+"F8.wireOp",EDGE,"E19.sketch_text.stroke-29")}),1.0]])]});
            var Q4;
            Q4=makeQuery(id+"F8.imprint","IMPRINT",FACE,{"disambiguationData":[TD([[makeQuery(id+"F8.imprint","IMPRINT",EDGE,{"derivedFrom":sQuery(id+"F8.wireOp",EDGE,"E19.sketch_text.stroke-36")}),1.0]])]});
            var Q5;
            Q5=makeQuery(id+"F8.imprint","IMPRINT",FACE,{"disambiguationData":[TD([[makeQuery(id+"F8.imprint","IMPRINT",EDGE,{"derivedFrom":sQuery(id+"F8.wireOp",EDGE,"E21.sketch_text.stroke-26")}),1.0]])]});
            var Q6;
            Q6=makeQuery(id+"F8.imprint","IMPRINT",FACE,{"disambiguationData":[TD([[makeQuery(id+"F8.imprint","IMPRINT",EDGE,{"derivedFrom":sQuery(id+"F8.wireOp",EDGE,"E15.sketch_text.stroke-22")}),1.0]])]});
            var Q7;
            Q7=makeQuery(id+"F8.imprint","IMPRINT",FACE,{"disambiguationData":[TD([[makeQuery(id+"F8.imprint","IMPRINT",EDGE,{"derivedFrom":sQuery(id+"F8.wireOp",EDGE,"E25.sketch_text.stroke-19")}),1.0]])]});
            var Q8;
            Q8=makeQuery(id+"F8.imprint","IMPRINT",FACE,{"disambiguationData":[TD([[makeQuery(id+"F8.imprint","IMPRINT",EDGE,{"derivedFrom":sQuery(id+"F8.wireOp",EDGE,"E23.sketch_text.stroke-16")}),1.0]])]});
            var Q9;
            Q9=makeQuery(id+"F8.imprint","IMPRINT",FACE,{"disambiguationData":[TD([[makeQuery(id+"F8.imprint","IMPRINT",EDGE,{"derivedFrom":sQuery(id+"F8.wireOp",EDGE,"E20.sketch_text.stroke-18")}),1.0]])]});
            var Q10;
            Q10=makeQuery(id+"F8.imprint","IMPRINT",FACE,{"disambiguationData":[TD([[makeQuery(id+"F8.imprint","IMPRINT",EDGE,{"derivedFrom":sQuery(id+"F8.wireOp",EDGE,"E20.sketch_text.stroke-25")}),1.0]])]});
            var Q11;
            Q11=makeQuery(id+"F8.imprint","IMPRINT",FACE,{"disambiguationData":[TD([[makeQuery(id+"F8.imprint","IMPRINT",EDGE,{"derivedFrom":sQuery(id+"F8.wireOp",EDGE,"E29.sketch_text.stroke-15")}),1.0]])]});
            var Q12;
            Q12=makeQuery(id+"F8.imprint","IMPRINT",FACE,{"disambiguationData":[TD([[makeQuery(id+"F8.imprint","IMPRINT",EDGE,{"derivedFrom":sQuery(id+"F8.wireOp",EDGE,"E26.sketch_text.stroke-8")}),1.0]])]});
            var Q13;
            Q13=makeQuery(id+"F8.imprint","IMPRINT",FACE,{"disambiguationData":[TD([[makeQuery(id+"F8.imprint","IMPRINT",EDGE,{"derivedFrom":sQuery(id+"F8.wireOp",EDGE,"E27.sketch_text.stroke-11")}),1.0]])]});
            extrude(context, id + "F9", {"entities" : qUnion([Q0, Q1, Q2, Q3, Q4, Q5, Q6, Q7, Q8, Q9, Q10, Q11, Q12, Q13]), "depth" : 0.25 * mm});
        }
        {
            var Q0;
            Q0=qCreatedBy(makeId("Top.planeOp"),FACE);
            cPlane(context, id + "F10", {"entities" : qUnion([Q0]), "cplaneType" : CPlaneType.OFFSET, "offset" : 2.38 * mm, "oppositeDirection" : true, "width" : 152.4 * mm, "height" : 152.4 * mm});
        }
        {
            var Q0;
            Q0=makeQuery(id+"F0.imprint","IMPRINT",FACE,{"disambiguationData":[TD([[makeQuery(id+"F0.imprint","IMPRINT",EDGE,{"derivedFrom":sQuery(id+"F0.wireOp",EDGE,"E0")}),-1.0]])]});
            var sketch = newSketch(context, id + "F11", { "sketchPlane" : qUnion([Q0])});
            skArc(sketch, "E83.0", {"start": v(-31.75, 75.95) * mm, "mid": v(-26.04, 70.23) * mm, "end": v(-31.75, 64.52) * mm});
            skLineSegment(sketch, "E83.1", {"start": v(-38.1, 75.95) * mm, "end": v(-31.75, 75.95) * mm});
            skArc(sketch, "E83.2", {"start": v(-38.1, -75.95) * mm, "mid": v(-114.05, 0) * mm, "end": v(-38.1, 75.95) * mm});
            skArc(sketch, "E83.3", {"start": v(-38.1, -64.52) * mm, "mid": v(-102.62, 0) * mm, "end": v(-38.1, 64.52) * mm});
            skLineSegment(sketch, "E83.4", {"start": v(-38.1, 64.52) * mm, "end": v(-31.75, 64.52) * mm});
            skLineSegment(sketch, "E83.5", {"start": v(-38.1, -64.52) * mm, "end": v(-36.58, -64.52) * mm});
            skArc(sketch, "E83.6", {"start": v(-36.58, -64.52) * mm, "mid": v(-30.86, -70.23) * mm, "end": v(-36.58, -75.95) * mm});
            skLineSegment(sketch, "E83.7", {"start": v(-38.1, -75.95) * mm, "end": v(-36.58, -75.95) * mm});
            skText(sketch, "E84", { "text": "0", "fontName": "Arimo-Regular.ttf"});
            skText(sketch, "E85", { "text": "1", "fontName": "Arimo-Regular.ttf"});
            skText(sketch, "E86", { "text": "2", "fontName": "Arimo-Regular.ttf"});
            skText(sketch, "E87", { "text": "3", "fontName": "Arimo-Regular.ttf"});
            skText(sketch, "E88", { "text": "4", "fontName": "Arimo-Regular.ttf"});
            skText(sketch, "E89", { "text": "5", "fontName": "Arimo-Regular.ttf"});
            skText(sketch, "E90", { "text": "6", "fontName": "Arimo-Regular.ttf"});
            skText(sketch, "E91", { "text": "7", "fontName": "Arimo-Regular.ttf"});
            skText(sketch, "E92", { "text": "8", "fontName": "Arimo-Regular.ttf"});
            skText(sketch, "E93", { "text": "9", "fontName": "Arimo-Regular.ttf"});
            skText(sketch, "E94", { "text": "10", "fontName": "Arimo-Regular.ttf"});
            skText(sketch, "E95", { "text": "11", "fontName": "Arimo-Regular.ttf"});
            skText(sketch, "E96", { "text": "12", "fontName": "Arimo-Regular.ttf"});
            skText(sketch, "E97", { "text": "13", "fontName": "Arimo-Regular.ttf"});
            skText(sketch, "E98", { "text": "14", "fontName": "Arimo-Regular.ttf"});
            skText(sketch, "E99", { "text": "15", "fontName": "Arimo-Regular.ttf"});
            skText(sketch, "E100", { "text": "16", "fontName": "Arimo-Regular.ttf"});
            skText(sketch, "E101", { "text": "17", "fontName": "Arimo-Regular.ttf"});
            skText(sketch, "E102", { "text": "18", "fontName": "Arimo-Regular.ttf"});
            skText(sketch, "E103", { "text": "19", "fontName": "Arimo-Regular.ttf"});
            skText(sketch, "E104", { "text": "20", "fontName": "Arimo-Regular.ttf"});
            skText(sketch, "E105", { "text": "21", "fontName": "Arimo-Regular.ttf"});
            const initialGuessF11  = {"E84": [-0.04006, -0.07216, 1, 0, 0.00491], "E85": [-0.0507, -0.07213, 1, 0, 0.00501], "E86": [-0.0608, -0.0697, 1, 0, 0.005], "E87": [-0.07058, -0.0659, 1, 0, 0.00488], "E88": [-0.07974, -0.06067, 1, 0, 0.00485], "E89": [-0.08784, -0.05405, 1, 0, 0.0049], "E90": [-0.09491, -0.04641, 1, 0, 0.0049], "E91": [-0.10075, -0.03742, 1, 0, 0.005], "E92": [-0.10594, -0.02813, 1, 0, 0.00496], "E93": [-0.10862, -0.0183, 1, 0, 0.00508], "E94": [-0.11236, -0.0079, 1, 0, 0.0051], "E95": [-0.11233, 0.00187, 1, 0, 0.00505], "E96": [-0.11048, 0.0132, 1, 0, 0.00505], "E97": [-0.10716, 0.02323, 1, 0, 0.00502], "E98": [-0.10307, 0.03278, 1, 0, 0.00502], "E99": [-0.09687, 0.04126, 1, 0, 0.00502], "E100": [-0.08949, 0.04905, 1, 0, 0.0051], "E101": [-0.08147, 0.05538, 1, 0, 0.00516], "E102": [-0.07232, 0.06092, 1, 0, 0.00505], "E103": [-0.06232, 0.06481, 1, 0, 0.00507], "E104": [-0.05226, 0.06715, 1, 0, 0.00502], "E105": [-0.04187, 0.0679, 1, 0, 0.0051]};
            skSetInitialGuess(sketch, initialGuessF11);
            skSolve(sketch);
        }
        {
            var Q0;
            Q0 = qSketchRegion(id + "F11", true);
            extrude(context, id + "F12", {"entities" : qUnion([Q0]), "depth" : 0.25 * mm});
        }
        {
            var Q0;
            Q0=makeQuery(id+"F11.imprint","IMPRINT",FACE,{"disambiguationData":[TD([[makeQuery(id+"F11.imprint","IMPRINT",EDGE,{"derivedFrom":sQuery(id+"F11.wireOp",EDGE,"E104.sketch_text.stroke-32")}),1.0]])]});
            var Q1;
            Q1=makeQuery(id+"F11.imprint","IMPRINT",FACE,{"disambiguationData":[TD([[makeQuery(id+"F11.imprint","IMPRINT",EDGE,{"derivedFrom":sQuery(id+"F11.wireOp",EDGE,"E103.sketch_text.stroke-27")}),1.0]])]});
            var Q2;
            Q2=makeQuery(id+"F11.imprint","IMPRINT",FACE,{"disambiguationData":[TD([[makeQuery(id+"F11.imprint","IMPRINT",EDGE,{"derivedFrom":sQuery(id+"F11.wireOp",EDGE,"E102.sketch_text.stroke-36")}),1.0]])]});
            var Q3;
            Q3=makeQuery(id+"F11.imprint","IMPRINT",FACE,{"disambiguationData":[TD([[makeQuery(id+"F11.imprint","IMPRINT",EDGE,{"derivedFrom":sQuery(id+"F11.wireOp",EDGE,"E102.sketch_text.stroke-29")}),1.0]])]});
            var Q4;
            Q4=makeQuery(id+"F11.imprint","IMPRINT",FACE,{"disambiguationData":[TD([[makeQuery(id+"F11.imprint","IMPRINT",EDGE,{"derivedFrom":sQuery(id+"F11.wireOp",EDGE,"E100.sketch_text.stroke-26")}),1.0]])]});
            var Q5;
            Q5=makeQuery(id+"F11.imprint","IMPRINT",FACE,{"disambiguationData":[TD([[makeQuery(id+"F11.imprint","IMPRINT",EDGE,{"derivedFrom":sQuery(id+"F11.wireOp",EDGE,"E98.sketch_text.stroke-22")}),1.0]])]});
            var Q6;
            Q6=makeQuery(id+"F11.imprint","IMPRINT",FACE,{"disambiguationData":[TD([[makeQuery(id+"F11.imprint","IMPRINT",EDGE,{"derivedFrom":sQuery(id+"F11.wireOp",EDGE,"E94.sketch_text.stroke-19")}),1.0]])]});
            var Q7;
            Q7=makeQuery(id+"F11.imprint","IMPRINT",FACE,{"disambiguationData":[TD([[makeQuery(id+"F11.imprint","IMPRINT",EDGE,{"derivedFrom":sQuery(id+"F11.wireOp",EDGE,"E93.sketch_text.stroke-16")}),1.0]])]});
            var Q8;
            Q8=makeQuery(id+"F11.imprint","IMPRINT",FACE,{"disambiguationData":[TD([[makeQuery(id+"F11.imprint","IMPRINT",EDGE,{"derivedFrom":sQuery(id+"F11.wireOp",EDGE,"E92.sketch_text.stroke-18")}),1.0]])]});
            var Q9;
            Q9=makeQuery(id+"F11.imprint","IMPRINT",FACE,{"disambiguationData":[TD([[makeQuery(id+"F11.imprint","IMPRINT",EDGE,{"derivedFrom":sQuery(id+"F11.wireOp",EDGE,"E92.sketch_text.stroke-25")}),1.0]])]});
            var Q10;
            Q10=makeQuery(id+"F11.imprint","IMPRINT",FACE,{"disambiguationData":[TD([[makeQuery(id+"F11.imprint","IMPRINT",EDGE,{"derivedFrom":sQuery(id+"F11.wireOp",EDGE,"E90.sketch_text.stroke-15")}),1.0]])]});
            var Q11;
            Q11=makeQuery(id+"F11.imprint","IMPRINT",FACE,{"disambiguationData":[TD([[makeQuery(id+"F11.imprint","IMPRINT",EDGE,{"derivedFrom":sQuery(id+"F11.wireOp",EDGE,"E88.sketch_text.stroke-11")}),1.0]])]});
            var Q12;
            Q12=makeQuery(id+"F11.imprint","IMPRINT",FACE,{"disambiguationData":[TD([[makeQuery(id+"F11.imprint","IMPRINT",EDGE,{"derivedFrom":sQuery(id+"F11.wireOp",EDGE,"E84.sketch_text.stroke-8")}),1.0]])]});
            extrude(context, id + "F13", {"entities" : qUnion([Q0, Q1, Q2, Q3, Q4, Q5, Q6, Q7, Q8, Q9, Q10, Q11, Q12]), "operationType" : NewBodyOperationType.ADD, "depth" : 0.25 * mm});
        }
    });
